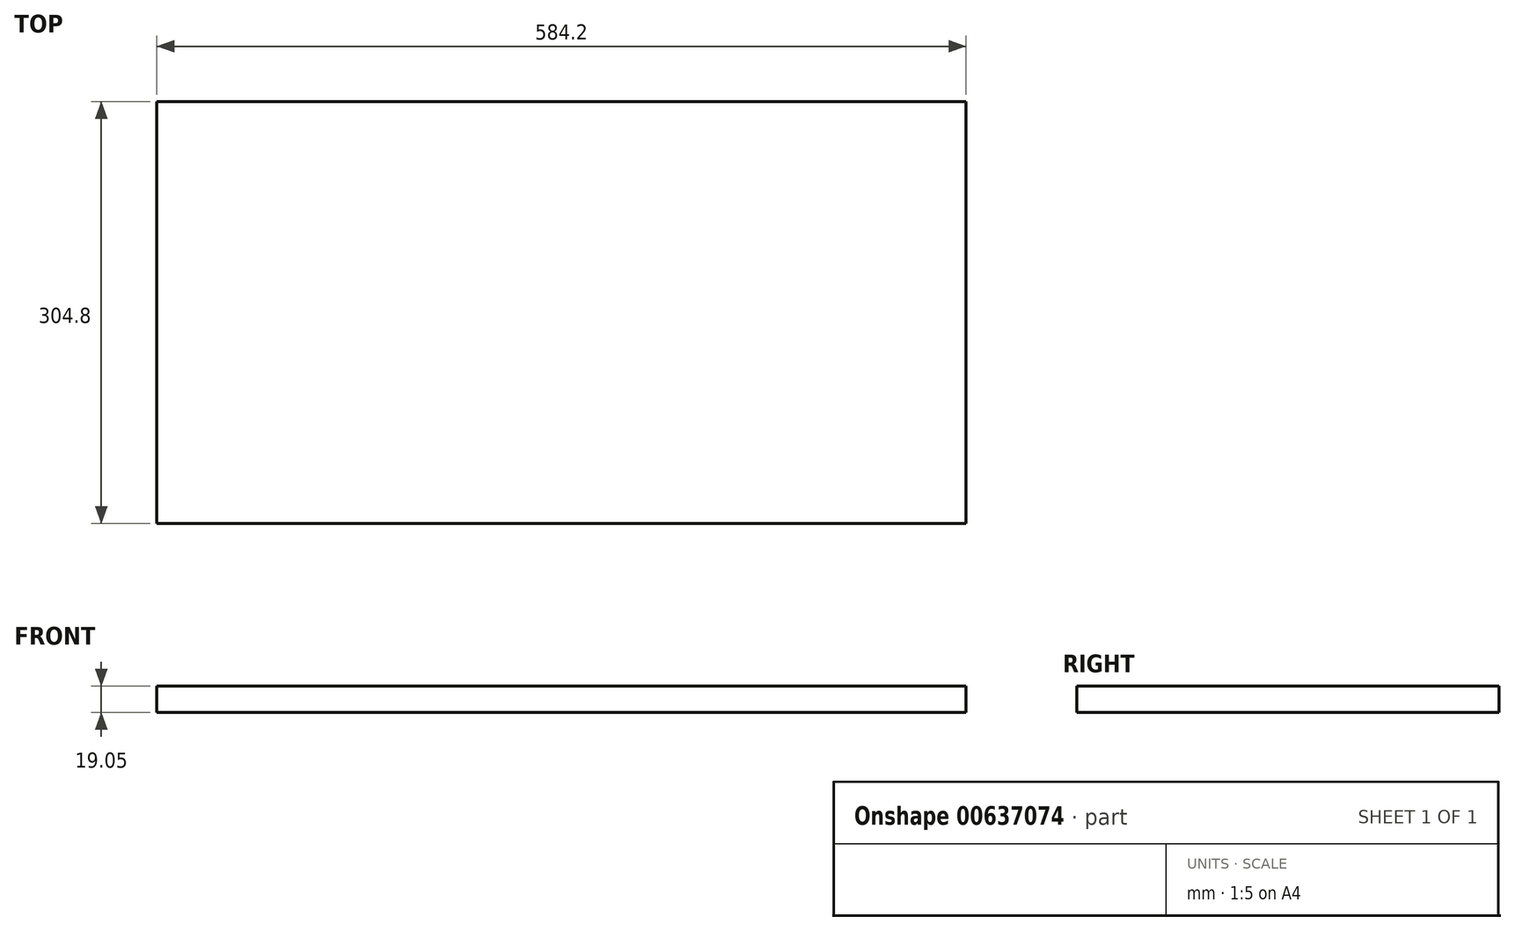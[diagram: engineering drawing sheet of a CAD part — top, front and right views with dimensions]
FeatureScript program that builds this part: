
annotation { "Feature Type Name" : "Feature", "Feature Type Description" : "" }
export const myFeature = defineFeature(function(context is Context, id is Id, definition is map)
    precondition{}
    {
        {
            var Q0;
            Q0=qCreatedBy(makeId("Top.planeOp"),FACE);
            var sketch = newSketch(context, id + "F0", { "sketchPlane" : qUnion([Q0])});
            skLineSegment(sketch, "E0.bottom", {"start": v(-339.63, 167.91) * mm, "end": v(244.57, 167.91) * mm});
            skLineSegment(sketch, "E0.top", {"start": v(-339.63, -136.89) * mm, "end": v(244.57, -136.89) * mm});
            skLineSegment(sketch, "E0.left", {"start": v(-339.63, 167.91) * mm, "end": v(-339.63, -136.89) * mm});
            skLineSegment(sketch, "E0.right", {"start": v(244.57, 167.91) * mm, "end": v(244.57, -136.89) * mm});
            skSolve(sketch);
        }
        {
            var Q0;
            Q0=makeQuery(id+"F0.imprint","IMPRINT",FACE,{"disambiguationData":[TD([[makeQuery(id+"F0.imprint","IMPRINT",EDGE,{"derivedFrom":sQuery(id+"F0.wireOp",EDGE,"E0.bottom")}),-1.0]])]});
            extrude(context, id + "F1", {"entities" : qUnion([Q0]), "depth" : 19.05 * mm, "offsetDistance" : 25.4 * mm});
        }
    });
